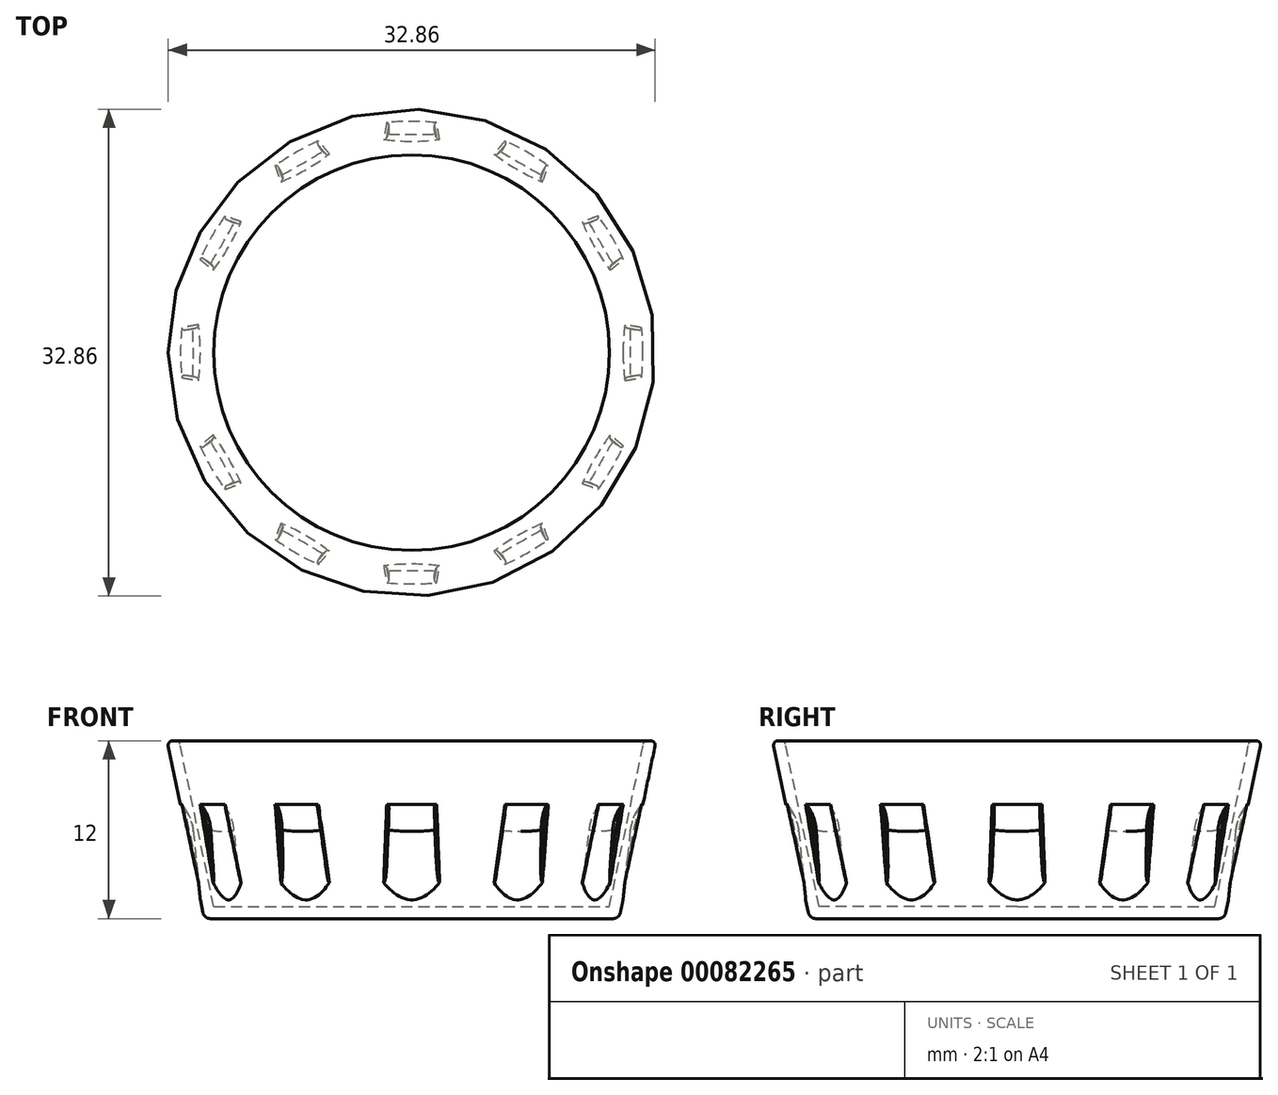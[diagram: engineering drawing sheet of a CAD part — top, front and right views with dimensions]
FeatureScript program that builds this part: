
annotation { "Feature Type Name" : "Feature", "Feature Type Description" : "" }
export const myFeature = defineFeature(function(context is Context, id is Id, definition is map)
    precondition{}
    {
        {
            var Q0;
            Q0=qCreatedBy(makeId("Front.planeOp"),FACE);
            var sketch = newSketch(context, id + "F0", { "sketchPlane" : qUnion([Q0])});
            skLineSegment(sketch, "E0", {"start": v(0, 0) * mm, "end": v(0, 12) * mm});
            skLineSegment(sketch, "E1.bottom", {"start": v(0, 12) * mm, "end": v(16.5, 12) * mm});
            skLineSegment(sketch, "E2", {"start": v(0, 0) * mm, "end": v(14, 0) * mm});
            skLineSegment(sketch, "E3", {"start": v(16.5, 12) * mm, "end": v(14, 0) * mm});
            skSolve(sketch);
        }
        {
            var Q0;
            Q0=qSketchRegion(id+"F0",true);
            var Q1;
            Q1=sQuery(id+"F0.wireOp",EDGE,"E0");
            revolve(context, id + "F1", {"entities" : qUnion([Q0]), "axis" : qUnion([Q1]), "revolveType" : RevolveType.FULL});
        }
        {
            var Q0;
            Q0=makeQuery(id+"F1.opRevolve","SWEPT_FACE",FACE,{"disambiguationData":[OSD([sQuery(id+"F0.wireOp",EDGE,"E1.bottom")])]});
            shell(context, id + "F2", {"entities" : qUnion([Q0]), "thickness" : 0.8 * mm});
        }
        {
            var Q0;
            Q0=makeQuery(id+"F2.opShell","OFFSET_EDGE",EDGE,{"disambiguationData":[OSD([sQuery(id+"F0.wireOp",EDGE,"E1.bottom"),sQuery(id+"F0.wireOp",EDGE,"E3")])]});
            var Q1;
            Q1=makeQuery(id+"F1.opRevolve","SWEPT_EDGE",EDGE,{"disambiguationData":[OSD([sQuery(id+"F0.wireOp",EDGE,"E1.bottom"),sQuery(id+"F0.wireOp",EDGE,"E3")])]});
            fillet(context, id + "F3", {"entities" : qUnion([Q0, Q1]), "radius" : .3 * mm, "tangentPropagation" : true, "allowEdgeOverflow" : false});
        }
        {
            var Q0;
            Q0=makeQuery(id+"F1.opRevolve","SWEPT_EDGE",EDGE,{"disambiguationData":[OSD([sQuery(id+"F0.wireOp",EDGE,"E2"),sQuery(id+"F0.wireOp",EDGE,"E3")])]});
            fillet(context, id + "F4", {"entities" : qUnion([Q0]), "radius" : .5 * mm, "tangentPropagation" : true, "allowEdgeOverflow" : false});
        }
        {
            var Q0;
            Q0=qCreatedBy(makeId("Front.planeOp"),FACE);
            var sketch = newSketch(context, id + "F5", { "sketchPlane" : qUnion([Q0])});
            skLineSegment(sketch, "E4", {"start": v(15.46, 12.9) * mm, "end": v(14.13, 0) * mm, "construction": true});
            skSolve(sketch);
        }
        {
            var Q0;
            Q0=sQuery(id+"F5.wireOp",EDGE,"E4");
            cPlane(context, id + "F6", {"entities" : qUnion([Q0]), "cplaneType" : CPlaneType.LINE_ANGLE, "offset" : 150 * mm, "angle" : 0 * degree, "width" : 150 * mm, "height" : 150 * mm});
        }
        {
            var Q0;
            Q0=qCreatedBy(id+"F6.planeOp",FACE);
            var sketch = newSketch(context, id + "F7", { "sketchPlane" : qUnion([Q0])});
            skPoint(sketch, "E5.middle", {"position": v(0, 9.22) * mm});
            skLineSegment(sketch, "E6.top", {"start": v(-1.5, 9.22) * mm, "end": v(1.5, 9.22) * mm});
            skLineSegment(sketch, "E7", {"start": v(1.5, 9.22) * mm, "end": v(1.8, 2.22) * mm});
            skLineSegment(sketch, "E8.MirrorCS", {"start": v(-1.5, 9.22) * mm, "end": v(-1.8, 2.22) * mm});
            skLineSegment(sketch, "E9", {"start": v(1.8, 2.22) * mm, "end": v(-1.8, 2.22) * mm});
            skSolve(sketch);
        }
        {
            var Q0;
            Q0=makeQuery(id+"F7.imprint","IMPRINT",FACE,{"disambiguationData":[TD([[makeQuery(id+"F7.imprint","IMPRINT",EDGE,{"derivedFrom":sQuery(id+"F7.wireOp",EDGE,"E6.top")}),-1.0]])]});
            extrude(context, id + "F8", {"entities" : qUnion([Q0]), "oppositeDirection" : true, "depth" : 1.04 * mm, "hasDraft" : true, "draftAngle" : 3 * degree});
        }
        {
            var Q0;
            Q0=makeQuery(id+"F8.opExtrude","SWEPT_BODY",BODY,{"disambiguationData":[OSD([sQuery(id+"F7.wireOp",EDGE,"E6.top"),sQuery(id+"F7.wireOp",EDGE,"E7"),sQuery(id+"F7.wireOp",EDGE,"E8.MirrorCS"),sQuery(id+"F7.wireOp",EDGE,"E9")])]});
            var Q1;
            {var subQ0=sQuery(id+"F0.wireOp",EDGE,"E3");Q1=makeQuery(id+"F4.opFillet","BLEND_EDGE",EDGE,{"blendedFrom":[makeQuery(id+"F1.opRevolve","SWEPT_EDGE",EDGE,{"disambiguationData":[OSD([sQuery(id+"F0.wireOp",EDGE,"E2"),subQ0])]}),makeQuery(id+"F1.opRevolve","SWEPT_FACE",FACE,{"disambiguationData":[OSD([subQ0])]})],"blendedInto":[makeQuery(id+"F1.opRevolve","SWEPT_FACE",FACE,{"disambiguationData":[OSD([subQ0])]})]});}
            circularPattern(context, id + "F9", {"entities" : qUnion([Q0]), "axis" : qUnion([Q1]), "angle" : 30 * degree, "instanceCount" : 12});
        }
        {
            var Q0;
            Q0=makeQuery(id+"F9.opPattern","COPY",BODY,{"derivedFrom":makeQuery(id+"F8.opExtrude","SWEPT_BODY",BODY,{"disambiguationData":[OSD([sQuery(id+"F7.wireOp",EDGE,"E6.top"),sQuery(id+"F7.wireOp",EDGE,"E7"),sQuery(id+"F7.wireOp",EDGE,"E8.MirrorCS"),sQuery(id+"F7.wireOp",EDGE,"E9")])]}),"instanceName":"17"});
            var Q1;
            Q1=makeQuery(id+"F9.opPattern","COPY",BODY,{"derivedFrom":makeQuery(id+"F8.opExtrude","SWEPT_BODY",BODY,{"disambiguationData":[OSD([sQuery(id+"F7.wireOp",EDGE,"E6.top"),sQuery(id+"F7.wireOp",EDGE,"E7"),sQuery(id+"F7.wireOp",EDGE,"E8.MirrorCS"),sQuery(id+"F7.wireOp",EDGE,"E9")])]}),"instanceName":"16"});
            var Q2;
            Q2=makeQuery(id+"F9.opPattern","COPY",BODY,{"derivedFrom":makeQuery(id+"F8.opExtrude","SWEPT_BODY",BODY,{"disambiguationData":[OSD([sQuery(id+"F7.wireOp",EDGE,"E6.top"),sQuery(id+"F7.wireOp",EDGE,"E7"),sQuery(id+"F7.wireOp",EDGE,"E8.MirrorCS"),sQuery(id+"F7.wireOp",EDGE,"E9")])]}),"instanceName":"15"});
            var Q3;
            Q3=makeQuery(id+"F9.opPattern","COPY",BODY,{"derivedFrom":makeQuery(id+"F8.opExtrude","SWEPT_BODY",BODY,{"disambiguationData":[OSD([sQuery(id+"F7.wireOp",EDGE,"E6.top"),sQuery(id+"F7.wireOp",EDGE,"E7"),sQuery(id+"F7.wireOp",EDGE,"E8.MirrorCS"),sQuery(id+"F7.wireOp",EDGE,"E9")])]}),"instanceName":"14"});
            var Q4;
            Q4=makeQuery(id+"F9.opPattern","COPY",BODY,{"derivedFrom":makeQuery(id+"F8.opExtrude","SWEPT_BODY",BODY,{"disambiguationData":[OSD([sQuery(id+"F7.wireOp",EDGE,"E6.top"),sQuery(id+"F7.wireOp",EDGE,"E7"),sQuery(id+"F7.wireOp",EDGE,"E8.MirrorCS"),sQuery(id+"F7.wireOp",EDGE,"E9")])]}),"instanceName":"13"});
            var Q5;
            Q5=makeQuery(id+"F9.opPattern","COPY",BODY,{"derivedFrom":makeQuery(id+"F8.opExtrude","SWEPT_BODY",BODY,{"disambiguationData":[OSD([sQuery(id+"F7.wireOp",EDGE,"E6.top"),sQuery(id+"F7.wireOp",EDGE,"E7"),sQuery(id+"F7.wireOp",EDGE,"E8.MirrorCS"),sQuery(id+"F7.wireOp",EDGE,"E9")])]}),"instanceName":"12"});
            var Q6;
            Q6=makeQuery(id+"F9.opPattern","COPY",BODY,{"derivedFrom":makeQuery(id+"F8.opExtrude","SWEPT_BODY",BODY,{"disambiguationData":[OSD([sQuery(id+"F7.wireOp",EDGE,"E6.top"),sQuery(id+"F7.wireOp",EDGE,"E7"),sQuery(id+"F7.wireOp",EDGE,"E8.MirrorCS"),sQuery(id+"F7.wireOp",EDGE,"E9")])]}),"instanceName":"11"});
            var Q7;
            Q7=makeQuery(id+"F9.opPattern","COPY",BODY,{"derivedFrom":makeQuery(id+"F8.opExtrude","SWEPT_BODY",BODY,{"disambiguationData":[OSD([sQuery(id+"F7.wireOp",EDGE,"E6.top"),sQuery(id+"F7.wireOp",EDGE,"E7"),sQuery(id+"F7.wireOp",EDGE,"E8.MirrorCS"),sQuery(id+"F7.wireOp",EDGE,"E9")])]}),"instanceName":"10"});
            var Q8;
            Q8=makeQuery(id+"F9.opPattern","COPY",BODY,{"derivedFrom":makeQuery(id+"F8.opExtrude","SWEPT_BODY",BODY,{"disambiguationData":[OSD([sQuery(id+"F7.wireOp",EDGE,"E6.top"),sQuery(id+"F7.wireOp",EDGE,"E7"),sQuery(id+"F7.wireOp",EDGE,"E8.MirrorCS"),sQuery(id+"F7.wireOp",EDGE,"E9")])]}),"instanceName":"9"});
            var Q9;
            Q9=makeQuery(id+"F9.opPattern","COPY",BODY,{"derivedFrom":makeQuery(id+"F8.opExtrude","SWEPT_BODY",BODY,{"disambiguationData":[OSD([sQuery(id+"F7.wireOp",EDGE,"E6.top"),sQuery(id+"F7.wireOp",EDGE,"E7"),sQuery(id+"F7.wireOp",EDGE,"E8.MirrorCS"),sQuery(id+"F7.wireOp",EDGE,"E9")])]}),"instanceName":"8"});
            var Q10;
            Q10=makeQuery(id+"F9.opPattern","COPY",BODY,{"derivedFrom":makeQuery(id+"F8.opExtrude","SWEPT_BODY",BODY,{"disambiguationData":[OSD([sQuery(id+"F7.wireOp",EDGE,"E6.top"),sQuery(id+"F7.wireOp",EDGE,"E7"),sQuery(id+"F7.wireOp",EDGE,"E8.MirrorCS"),sQuery(id+"F7.wireOp",EDGE,"E9")])]}),"instanceName":"7"});
            var Q11;
            Q11=makeQuery(id+"F9.opPattern","COPY",BODY,{"derivedFrom":makeQuery(id+"F8.opExtrude","SWEPT_BODY",BODY,{"disambiguationData":[OSD([sQuery(id+"F7.wireOp",EDGE,"E6.top"),sQuery(id+"F7.wireOp",EDGE,"E7"),sQuery(id+"F7.wireOp",EDGE,"E8.MirrorCS"),sQuery(id+"F7.wireOp",EDGE,"E9")])]}),"instanceName":"6"});
            var Q12;
            Q12=makeQuery(id+"F9.opPattern","COPY",BODY,{"derivedFrom":makeQuery(id+"F8.opExtrude","SWEPT_BODY",BODY,{"disambiguationData":[OSD([sQuery(id+"F7.wireOp",EDGE,"E6.top"),sQuery(id+"F7.wireOp",EDGE,"E7"),sQuery(id+"F7.wireOp",EDGE,"E8.MirrorCS"),sQuery(id+"F7.wireOp",EDGE,"E9")])]}),"instanceName":"5"});
            var Q13;
            Q13=makeQuery(id+"F9.opPattern","COPY",BODY,{"derivedFrom":makeQuery(id+"F8.opExtrude","SWEPT_BODY",BODY,{"disambiguationData":[OSD([sQuery(id+"F7.wireOp",EDGE,"E6.top"),sQuery(id+"F7.wireOp",EDGE,"E7"),sQuery(id+"F7.wireOp",EDGE,"E8.MirrorCS"),sQuery(id+"F7.wireOp",EDGE,"E9")])]}),"instanceName":"4"});
            var Q14;
            Q14=makeQuery(id+"F9.opPattern","COPY",BODY,{"derivedFrom":makeQuery(id+"F8.opExtrude","SWEPT_BODY",BODY,{"disambiguationData":[OSD([sQuery(id+"F7.wireOp",EDGE,"E6.top"),sQuery(id+"F7.wireOp",EDGE,"E7"),sQuery(id+"F7.wireOp",EDGE,"E8.MirrorCS"),sQuery(id+"F7.wireOp",EDGE,"E9")])]}),"instanceName":"3"});
            var Q15;
            Q15=makeQuery(id+"F9.opPattern","COPY",BODY,{"derivedFrom":makeQuery(id+"F8.opExtrude","SWEPT_BODY",BODY,{"disambiguationData":[OSD([sQuery(id+"F7.wireOp",EDGE,"E6.top"),sQuery(id+"F7.wireOp",EDGE,"E7"),sQuery(id+"F7.wireOp",EDGE,"E8.MirrorCS"),sQuery(id+"F7.wireOp",EDGE,"E9")])]}),"instanceName":"2"});
            var Q16;
            Q16=makeQuery(id+"F9.opPattern","COPY",BODY,{"derivedFrom":makeQuery(id+"F8.opExtrude","SWEPT_BODY",BODY,{"disambiguationData":[OSD([sQuery(id+"F7.wireOp",EDGE,"E6.top"),sQuery(id+"F7.wireOp",EDGE,"E7"),sQuery(id+"F7.wireOp",EDGE,"E8.MirrorCS"),sQuery(id+"F7.wireOp",EDGE,"E9")])]}),"instanceName":"1"});
            var Q17;
            Q17=makeQuery(id+"F8.opExtrude","SWEPT_BODY",BODY,{"disambiguationData":[OSD([sQuery(id+"F7.wireOp",EDGE,"E6.top"),sQuery(id+"F7.wireOp",EDGE,"E7"),sQuery(id+"F7.wireOp",EDGE,"E8.MirrorCS"),sQuery(id+"F7.wireOp",EDGE,"E9")])]});
            var Q18;
            Q18=makeQuery(id+"F1.opRevolve","SWEPT_BODY",BODY,{"disambiguationData":[OSD([sQuery(id+"F0.wireOp",EDGE,"E0"),sQuery(id+"F0.wireOp",EDGE,"E1.bottom"),sQuery(id+"F0.wireOp",EDGE,"E2"),sQuery(id+"F0.wireOp",EDGE,"E3")])]});
            booleanBodies(context, id + "F10", {"operationType" : BooleanOperationType.SUBTRACTION, "tools" : qUnion([Q0, Q1, Q2, Q3, Q4, Q5, Q6, Q7, Q8, Q9, Q10, Q11, Q12, Q13, Q14, Q15, Q16, Q17]), "targets" : qUnion([Q18])});
        }
        {
            var Q0;
            Q0=makeQuery(id+"F10.opBoolean","COPY",EDGE,{"derivedFrom":makeQuery(id+"F9.opPattern","COPY",EDGE,{"derivedFrom":makeQuery(id+"F8.opExtrude","CAP_EDGE",EDGE,{"disambiguationData":[OSD([sQuery(id+"F7.wireOp",EDGE,"E6.top")])],"isStart":true}),"instanceName":"6"})});
            var Q1;
            Q1=makeQuery(id+"F10.opBoolean","COPY",EDGE,{"derivedFrom":makeQuery(id+"F9.opPattern","COPY",EDGE,{"derivedFrom":makeQuery(id+"F8.opExtrude","CAP_EDGE",EDGE,{"disambiguationData":[OSD([sQuery(id+"F7.wireOp",EDGE,"E6.top")])],"isStart":true}),"instanceName":"7"})});
            var Q2;
            Q2=makeQuery(id+"F10.opBoolean","COPY",EDGE,{"derivedFrom":makeQuery(id+"F9.opPattern","COPY",EDGE,{"derivedFrom":makeQuery(id+"F8.opExtrude","CAP_EDGE",EDGE,{"disambiguationData":[OSD([sQuery(id+"F7.wireOp",EDGE,"E6.top")])],"isStart":true}),"instanceName":"5"})});
            var Q3;
            Q3=makeQuery(id+"F10.opBoolean","COPY",EDGE,{"derivedFrom":makeQuery(id+"F9.opPattern","COPY",EDGE,{"derivedFrom":makeQuery(id+"F8.opExtrude","CAP_EDGE",EDGE,{"disambiguationData":[OSD([sQuery(id+"F7.wireOp",EDGE,"E6.top")])],"isStart":true}),"instanceName":"4"})});
            var Q4;
            Q4=makeQuery(id+"F10.opBoolean","COPY",EDGE,{"derivedFrom":makeQuery(id+"F9.opPattern","COPY",EDGE,{"derivedFrom":makeQuery(id+"F8.opExtrude","CAP_EDGE",EDGE,{"disambiguationData":[OSD([sQuery(id+"F7.wireOp",EDGE,"E6.top")])],"isStart":true}),"instanceName":"8"})});
            var Q5;
            Q5=makeQuery(id+"F10.opBoolean","COPY",EDGE,{"derivedFrom":makeQuery(id+"F9.opPattern","COPY",EDGE,{"derivedFrom":makeQuery(id+"F8.opExtrude","CAP_EDGE",EDGE,{"disambiguationData":[OSD([sQuery(id+"F7.wireOp",EDGE,"E6.top")])],"isStart":true}),"instanceName":"9"})});
            var Q6;
            Q6=makeQuery(id+"F10.opBoolean","COPY",EDGE,{"derivedFrom":makeQuery(id+"F9.opPattern","COPY",EDGE,{"derivedFrom":makeQuery(id+"F8.opExtrude","CAP_EDGE",EDGE,{"disambiguationData":[OSD([sQuery(id+"F7.wireOp",EDGE,"E6.top")])],"isStart":true}),"instanceName":"10"})});
            var Q7;
            Q7=makeQuery(id+"F10.opBoolean","COPY",EDGE,{"derivedFrom":makeQuery(id+"F9.opPattern","COPY",EDGE,{"derivedFrom":makeQuery(id+"F8.opExtrude","CAP_EDGE",EDGE,{"disambiguationData":[OSD([sQuery(id+"F7.wireOp",EDGE,"E6.top")])],"isStart":true}),"instanceName":"11"})});
            var Q8;
            Q8=makeQuery(id+"F10.opBoolean","COPY",EDGE,{"derivedFrom":makeQuery(id+"F9.opPattern","COPY",EDGE,{"derivedFrom":makeQuery(id+"F8.opExtrude","CAP_EDGE",EDGE,{"disambiguationData":[OSD([sQuery(id+"F7.wireOp",EDGE,"E6.top")])],"isStart":true}),"instanceName":"12"})});
            var Q9;
            Q9=makeQuery(id+"F10.opBoolean","COPY",EDGE,{"derivedFrom":makeQuery(id+"F9.opPattern","COPY",EDGE,{"derivedFrom":makeQuery(id+"F8.opExtrude","CAP_EDGE",EDGE,{"disambiguationData":[OSD([sQuery(id+"F7.wireOp",EDGE,"E6.top")])],"isStart":true}),"instanceName":"13"})});
            var Q10;
            Q10=makeQuery(id+"F10.opBoolean","COPY",EDGE,{"derivedFrom":makeQuery(id+"F9.opPattern","COPY",EDGE,{"derivedFrom":makeQuery(id+"F8.opExtrude","CAP_EDGE",EDGE,{"disambiguationData":[OSD([sQuery(id+"F7.wireOp",EDGE,"E6.top")])],"isStart":true}),"instanceName":"3"})});
            var Q11;
            Q11=makeQuery(id+"F10.opBoolean","COPY",EDGE,{"derivedFrom":makeQuery(id+"F9.opPattern","COPY",EDGE,{"derivedFrom":makeQuery(id+"F8.opExtrude","CAP_EDGE",EDGE,{"disambiguationData":[OSD([sQuery(id+"F7.wireOp",EDGE,"E6.top")])],"isStart":true}),"instanceName":"2"})});
            var Q12;
            Q12=makeQuery(id+"F10.opBoolean","COPY",EDGE,{"derivedFrom":makeQuery(id+"F9.opPattern","COPY",EDGE,{"derivedFrom":makeQuery(id+"F8.opExtrude","CAP_EDGE",EDGE,{"disambiguationData":[OSD([sQuery(id+"F7.wireOp",EDGE,"E6.top")])],"isStart":true}),"instanceName":"1"})});
            var Q13;
            Q13=makeQuery(id+"F10.opBoolean","COPY",EDGE,{"derivedFrom":makeQuery(id+"F8.opExtrude","CAP_EDGE",EDGE,{"disambiguationData":[OSD([sQuery(id+"F7.wireOp",EDGE,"E6.top")])],"isStart":true})});
            var Q14;
            Q14=makeQuery(id+"F10.opBoolean","COPY",EDGE,{"derivedFrom":makeQuery(id+"F9.opPattern","COPY",EDGE,{"derivedFrom":makeQuery(id+"F8.opExtrude","CAP_EDGE",EDGE,{"disambiguationData":[OSD([sQuery(id+"F7.wireOp",EDGE,"E6.top")])],"isStart":true}),"instanceName":"17"})});
            var Q15;
            Q15=makeQuery(id+"F10.opBoolean","COPY",EDGE,{"derivedFrom":makeQuery(id+"F9.opPattern","COPY",EDGE,{"derivedFrom":makeQuery(id+"F8.opExtrude","CAP_EDGE",EDGE,{"disambiguationData":[OSD([sQuery(id+"F7.wireOp",EDGE,"E6.top")])],"isStart":true}),"instanceName":"16"})});
            var Q16;
            Q16=makeQuery(id+"F10.opBoolean","COPY",EDGE,{"derivedFrom":makeQuery(id+"F9.opPattern","COPY",EDGE,{"derivedFrom":makeQuery(id+"F8.opExtrude","CAP_EDGE",EDGE,{"disambiguationData":[OSD([sQuery(id+"F7.wireOp",EDGE,"E6.top")])],"isStart":true}),"instanceName":"15"})});
            var Q17;
            Q17=makeQuery(id+"F10.opBoolean","COPY",EDGE,{"derivedFrom":makeQuery(id+"F9.opPattern","COPY",EDGE,{"derivedFrom":makeQuery(id+"F8.opExtrude","CAP_EDGE",EDGE,{"disambiguationData":[OSD([sQuery(id+"F7.wireOp",EDGE,"E6.top")])],"isStart":true}),"instanceName":"14"})});
            fillet(context, id + "F11", {"entities" : qUnion([Q0, Q1, Q2, Q3, Q4, Q5, Q6, Q7, Q8, Q9, Q10, Q11, Q12, Q13, Q14, Q15, Q16, Q17]), "radius" : 3 * mm, "tangentPropagation" : true, "allowEdgeOverflow" : false});
        }
        {
            var Q0;
            Q0=makeQuery(id+"F10.opBoolean","INTERSECT",EDGE,{"derivedFrom":[makeQuery(id+"F1.opRevolve","SWEPT_FACE",FACE,{"disambiguationData":[OSD([sQuery(id+"F0.wireOp",EDGE,"E3")])]}),makeQuery(id+"F9.opPattern","COPY",FACE,{"derivedFrom":makeQuery(id+"F8.opExtrude","SWEPT_FACE",FACE,{"disambiguationData":[OSD([sQuery(id+"F7.wireOp",EDGE,"E8.MirrorCS")])]}),"instanceName":"2"})]});
            var Q1;
            Q1=makeQuery(id+"F10.opBoolean","INTERSECT",EDGE,{"derivedFrom":[makeQuery(id+"F1.opRevolve","SWEPT_FACE",FACE,{"disambiguationData":[OSD([sQuery(id+"F0.wireOp",EDGE,"E3")])]}),makeQuery(id+"F9.opPattern","COPY",FACE,{"derivedFrom":makeQuery(id+"F8.opExtrude","SWEPT_FACE",FACE,{"disambiguationData":[OSD([sQuery(id+"F7.wireOp",EDGE,"E7")])]}),"instanceName":"2"})]});
            var Q2;
            Q2=makeQuery(id+"F10.opBoolean","INTERSECT",EDGE,{"derivedFrom":[makeQuery(id+"F1.opRevolve","SWEPT_FACE",FACE,{"disambiguationData":[OSD([sQuery(id+"F0.wireOp",EDGE,"E3")])]}),makeQuery(id+"F9.opPattern","COPY",FACE,{"derivedFrom":makeQuery(id+"F8.opExtrude","SWEPT_FACE",FACE,{"disambiguationData":[OSD([sQuery(id+"F7.wireOp",EDGE,"E8.MirrorCS")])]}),"instanceName":"3"})]});
            var Q3;
            Q3=makeQuery(id+"F10.opBoolean","INTERSECT",EDGE,{"derivedFrom":[makeQuery(id+"F1.opRevolve","SWEPT_FACE",FACE,{"disambiguationData":[OSD([sQuery(id+"F0.wireOp",EDGE,"E3")])]}),makeQuery(id+"F9.opPattern","COPY",FACE,{"derivedFrom":makeQuery(id+"F8.opExtrude","SWEPT_FACE",FACE,{"disambiguationData":[OSD([sQuery(id+"F7.wireOp",EDGE,"E8.MirrorCS")])]}),"instanceName":"4"})]});
            var Q4;
            Q4=makeQuery(id+"F10.opBoolean","INTERSECT",EDGE,{"derivedFrom":[makeQuery(id+"F1.opRevolve","SWEPT_FACE",FACE,{"disambiguationData":[OSD([sQuery(id+"F0.wireOp",EDGE,"E3")])]}),makeQuery(id+"F9.opPattern","COPY",FACE,{"derivedFrom":makeQuery(id+"F8.opExtrude","SWEPT_FACE",FACE,{"disambiguationData":[OSD([sQuery(id+"F7.wireOp",EDGE,"E8.MirrorCS")])]}),"instanceName":"5"})]});
            var Q5;
            Q5=makeQuery(id+"F10.opBoolean","INTERSECT",EDGE,{"derivedFrom":[makeQuery(id+"F1.opRevolve","SWEPT_FACE",FACE,{"disambiguationData":[OSD([sQuery(id+"F0.wireOp",EDGE,"E3")])]}),makeQuery(id+"F9.opPattern","COPY",FACE,{"derivedFrom":makeQuery(id+"F8.opExtrude","SWEPT_FACE",FACE,{"disambiguationData":[OSD([sQuery(id+"F7.wireOp",EDGE,"E8.MirrorCS")])]}),"instanceName":"1"})]});
            var Q6;
            Q6=makeQuery(id+"F10.opBoolean","INTERSECT",EDGE,{"derivedFrom":[makeQuery(id+"F1.opRevolve","SWEPT_FACE",FACE,{"disambiguationData":[OSD([sQuery(id+"F0.wireOp",EDGE,"E3")])]}),makeQuery(id+"F9.opPattern","COPY",FACE,{"derivedFrom":makeQuery(id+"F8.opExtrude","SWEPT_FACE",FACE,{"disambiguationData":[OSD([sQuery(id+"F7.wireOp",EDGE,"E7")])]}),"instanceName":"1"})]});
            var Q7;
            Q7=makeQuery(id+"F10.opBoolean","INTERSECT",EDGE,{"derivedFrom":[makeQuery(id+"F1.opRevolve","SWEPT_FACE",FACE,{"disambiguationData":[OSD([sQuery(id+"F0.wireOp",EDGE,"E3")])]}),makeQuery(id+"F8.opExtrude","SWEPT_FACE",FACE,{"disambiguationData":[OSD([sQuery(id+"F7.wireOp",EDGE,"E7")])]})]});
            var Q8;
            Q8=makeQuery(id+"F10.opBoolean","INTERSECT",EDGE,{"derivedFrom":[makeQuery(id+"F1.opRevolve","SWEPT_FACE",FACE,{"disambiguationData":[OSD([sQuery(id+"F0.wireOp",EDGE,"E3")])]}),makeQuery(id+"F8.opExtrude","SWEPT_FACE",FACE,{"disambiguationData":[OSD([sQuery(id+"F7.wireOp",EDGE,"E8.MirrorCS")])]})]});
            var Q9;
            Q9=makeQuery(id+"F10.opBoolean","INTERSECT",EDGE,{"derivedFrom":[makeQuery(id+"F1.opRevolve","SWEPT_FACE",FACE,{"disambiguationData":[OSD([sQuery(id+"F0.wireOp",EDGE,"E3")])]}),makeQuery(id+"F9.opPattern","COPY",FACE,{"derivedFrom":makeQuery(id+"F8.opExtrude","SWEPT_FACE",FACE,{"disambiguationData":[OSD([sQuery(id+"F7.wireOp",EDGE,"E8.MirrorCS")])]}),"instanceName":"17"})]});
            var Q10;
            Q10=makeQuery(id+"F10.opBoolean","INTERSECT",EDGE,{"derivedFrom":[makeQuery(id+"F1.opRevolve","SWEPT_FACE",FACE,{"disambiguationData":[OSD([sQuery(id+"F0.wireOp",EDGE,"E3")])]}),makeQuery(id+"F9.opPattern","COPY",FACE,{"derivedFrom":makeQuery(id+"F8.opExtrude","SWEPT_FACE",FACE,{"disambiguationData":[OSD([sQuery(id+"F7.wireOp",EDGE,"E7")])]}),"instanceName":"17"})]});
            var Q11;
            Q11=makeQuery(id+"F10.opBoolean","INTERSECT",EDGE,{"derivedFrom":[makeQuery(id+"F1.opRevolve","SWEPT_FACE",FACE,{"disambiguationData":[OSD([sQuery(id+"F0.wireOp",EDGE,"E3")])]}),makeQuery(id+"F9.opPattern","COPY",FACE,{"derivedFrom":makeQuery(id+"F8.opExtrude","SWEPT_FACE",FACE,{"disambiguationData":[OSD([sQuery(id+"F7.wireOp",EDGE,"E7")])]}),"instanceName":"3"})]});
            var Q12;
            Q12=makeQuery(id+"F10.opBoolean","INTERSECT",EDGE,{"derivedFrom":[makeQuery(id+"F1.opRevolve","SWEPT_FACE",FACE,{"disambiguationData":[OSD([sQuery(id+"F0.wireOp",EDGE,"E3")])]}),makeQuery(id+"F9.opPattern","COPY",FACE,{"derivedFrom":makeQuery(id+"F8.opExtrude","SWEPT_FACE",FACE,{"disambiguationData":[OSD([sQuery(id+"F7.wireOp",EDGE,"E7")])]}),"instanceName":"4"})]});
            var Q13;
            Q13=makeQuery(id+"F10.opBoolean","INTERSECT",EDGE,{"derivedFrom":[makeQuery(id+"F1.opRevolve","SWEPT_FACE",FACE,{"disambiguationData":[OSD([sQuery(id+"F0.wireOp",EDGE,"E3")])]}),makeQuery(id+"F9.opPattern","COPY",FACE,{"derivedFrom":makeQuery(id+"F8.opExtrude","SWEPT_FACE",FACE,{"disambiguationData":[OSD([sQuery(id+"F7.wireOp",EDGE,"E7")])]}),"instanceName":"5"})]});
            var Q14;
            Q14=makeQuery(id+"F10.opBoolean","INTERSECT",EDGE,{"derivedFrom":[makeQuery(id+"F1.opRevolve","SWEPT_FACE",FACE,{"disambiguationData":[OSD([sQuery(id+"F0.wireOp",EDGE,"E3")])]}),makeQuery(id+"F9.opPattern","COPY",FACE,{"derivedFrom":makeQuery(id+"F8.opExtrude","SWEPT_FACE",FACE,{"disambiguationData":[OSD([sQuery(id+"F7.wireOp",EDGE,"E7")])]}),"instanceName":"6"})]});
            var Q15;
            Q15=makeQuery(id+"F10.opBoolean","INTERSECT",EDGE,{"derivedFrom":[makeQuery(id+"F1.opRevolve","SWEPT_FACE",FACE,{"disambiguationData":[OSD([sQuery(id+"F0.wireOp",EDGE,"E3")])]}),makeQuery(id+"F9.opPattern","COPY",FACE,{"derivedFrom":makeQuery(id+"F8.opExtrude","SWEPT_FACE",FACE,{"disambiguationData":[OSD([sQuery(id+"F7.wireOp",EDGE,"E8.MirrorCS")])]}),"instanceName":"6"})]});
            var Q16;
            Q16=makeQuery(id+"F10.opBoolean","INTERSECT",EDGE,{"derivedFrom":[makeQuery(id+"F1.opRevolve","SWEPT_FACE",FACE,{"disambiguationData":[OSD([sQuery(id+"F0.wireOp",EDGE,"E3")])]}),makeQuery(id+"F9.opPattern","COPY",FACE,{"derivedFrom":makeQuery(id+"F8.opExtrude","SWEPT_FACE",FACE,{"disambiguationData":[OSD([sQuery(id+"F7.wireOp",EDGE,"E7")])]}),"instanceName":"7"})]});
            var Q17;
            Q17=makeQuery(id+"F10.opBoolean","INTERSECT",EDGE,{"derivedFrom":[makeQuery(id+"F1.opRevolve","SWEPT_FACE",FACE,{"disambiguationData":[OSD([sQuery(id+"F0.wireOp",EDGE,"E3")])]}),makeQuery(id+"F9.opPattern","COPY",FACE,{"derivedFrom":makeQuery(id+"F8.opExtrude","SWEPT_FACE",FACE,{"disambiguationData":[OSD([sQuery(id+"F7.wireOp",EDGE,"E8.MirrorCS")])]}),"instanceName":"7"})]});
            var Q18;
            Q18=makeQuery(id+"F10.opBoolean","INTERSECT",EDGE,{"derivedFrom":[makeQuery(id+"F1.opRevolve","SWEPT_FACE",FACE,{"disambiguationData":[OSD([sQuery(id+"F0.wireOp",EDGE,"E3")])]}),makeQuery(id+"F9.opPattern","COPY",FACE,{"derivedFrom":makeQuery(id+"F8.opExtrude","SWEPT_FACE",FACE,{"disambiguationData":[OSD([sQuery(id+"F7.wireOp",EDGE,"E7")])]}),"instanceName":"8"})]});
            var Q19;
            Q19=makeQuery(id+"F10.opBoolean","INTERSECT",EDGE,{"derivedFrom":[makeQuery(id+"F1.opRevolve","SWEPT_FACE",FACE,{"disambiguationData":[OSD([sQuery(id+"F0.wireOp",EDGE,"E3")])]}),makeQuery(id+"F9.opPattern","COPY",FACE,{"derivedFrom":makeQuery(id+"F8.opExtrude","SWEPT_FACE",FACE,{"disambiguationData":[OSD([sQuery(id+"F7.wireOp",EDGE,"E8.MirrorCS")])]}),"instanceName":"8"})]});
            var Q20;
            Q20=makeQuery(id+"F10.opBoolean","INTERSECT",EDGE,{"derivedFrom":[makeQuery(id+"F1.opRevolve","SWEPT_FACE",FACE,{"disambiguationData":[OSD([sQuery(id+"F0.wireOp",EDGE,"E3")])]}),makeQuery(id+"F9.opPattern","COPY",FACE,{"derivedFrom":makeQuery(id+"F8.opExtrude","SWEPT_FACE",FACE,{"disambiguationData":[OSD([sQuery(id+"F7.wireOp",EDGE,"E7")])]}),"instanceName":"9"})]});
            var Q21;
            Q21=makeQuery(id+"F10.opBoolean","INTERSECT",EDGE,{"derivedFrom":[makeQuery(id+"F1.opRevolve","SWEPT_FACE",FACE,{"disambiguationData":[OSD([sQuery(id+"F0.wireOp",EDGE,"E3")])]}),makeQuery(id+"F9.opPattern","COPY",FACE,{"derivedFrom":makeQuery(id+"F8.opExtrude","SWEPT_FACE",FACE,{"disambiguationData":[OSD([sQuery(id+"F7.wireOp",EDGE,"E8.MirrorCS")])]}),"instanceName":"9"})]});
            var Q22;
            Q22=makeQuery(id+"F10.opBoolean","INTERSECT",EDGE,{"derivedFrom":[makeQuery(id+"F1.opRevolve","SWEPT_FACE",FACE,{"disambiguationData":[OSD([sQuery(id+"F0.wireOp",EDGE,"E3")])]}),makeQuery(id+"F9.opPattern","COPY",FACE,{"derivedFrom":makeQuery(id+"F8.opExtrude","SWEPT_FACE",FACE,{"disambiguationData":[OSD([sQuery(id+"F7.wireOp",EDGE,"E7")])]}),"instanceName":"10"})]});
            var Q23;
            Q23=makeQuery(id+"F10.opBoolean","INTERSECT",EDGE,{"derivedFrom":[makeQuery(id+"F1.opRevolve","SWEPT_FACE",FACE,{"disambiguationData":[OSD([sQuery(id+"F0.wireOp",EDGE,"E3")])]}),makeQuery(id+"F9.opPattern","COPY",FACE,{"derivedFrom":makeQuery(id+"F8.opExtrude","SWEPT_FACE",FACE,{"disambiguationData":[OSD([sQuery(id+"F7.wireOp",EDGE,"E8.MirrorCS")])]}),"instanceName":"10"})]});
            var Q24;
            Q24=makeQuery(id+"F10.opBoolean","INTERSECT",EDGE,{"derivedFrom":[makeQuery(id+"F1.opRevolve","SWEPT_FACE",FACE,{"disambiguationData":[OSD([sQuery(id+"F0.wireOp",EDGE,"E3")])]}),makeQuery(id+"F9.opPattern","COPY",FACE,{"derivedFrom":makeQuery(id+"F8.opExtrude","SWEPT_FACE",FACE,{"disambiguationData":[OSD([sQuery(id+"F7.wireOp",EDGE,"E7")])]}),"instanceName":"11"})]});
            var Q25;
            Q25=makeQuery(id+"F10.opBoolean","INTERSECT",EDGE,{"derivedFrom":[makeQuery(id+"F1.opRevolve","SWEPT_FACE",FACE,{"disambiguationData":[OSD([sQuery(id+"F0.wireOp",EDGE,"E3")])]}),makeQuery(id+"F9.opPattern","COPY",FACE,{"derivedFrom":makeQuery(id+"F8.opExtrude","SWEPT_FACE",FACE,{"disambiguationData":[OSD([sQuery(id+"F7.wireOp",EDGE,"E8.MirrorCS")])]}),"instanceName":"11"})]});
            var Q26;
            Q26=makeQuery(id+"F10.opBoolean","INTERSECT",EDGE,{"derivedFrom":[makeQuery(id+"F1.opRevolve","SWEPT_FACE",FACE,{"disambiguationData":[OSD([sQuery(id+"F0.wireOp",EDGE,"E3")])]}),makeQuery(id+"F9.opPattern","COPY",FACE,{"derivedFrom":makeQuery(id+"F8.opExtrude","SWEPT_FACE",FACE,{"disambiguationData":[OSD([sQuery(id+"F7.wireOp",EDGE,"E7")])]}),"instanceName":"12"})]});
            var Q27;
            Q27=makeQuery(id+"F10.opBoolean","INTERSECT",EDGE,{"derivedFrom":[makeQuery(id+"F1.opRevolve","SWEPT_FACE",FACE,{"disambiguationData":[OSD([sQuery(id+"F0.wireOp",EDGE,"E3")])]}),makeQuery(id+"F9.opPattern","COPY",FACE,{"derivedFrom":makeQuery(id+"F8.opExtrude","SWEPT_FACE",FACE,{"disambiguationData":[OSD([sQuery(id+"F7.wireOp",EDGE,"E8.MirrorCS")])]}),"instanceName":"12"})]});
            var Q28;
            Q28=makeQuery(id+"F10.opBoolean","INTERSECT",EDGE,{"derivedFrom":[makeQuery(id+"F1.opRevolve","SWEPT_FACE",FACE,{"disambiguationData":[OSD([sQuery(id+"F0.wireOp",EDGE,"E3")])]}),makeQuery(id+"F9.opPattern","COPY",FACE,{"derivedFrom":makeQuery(id+"F8.opExtrude","SWEPT_FACE",FACE,{"disambiguationData":[OSD([sQuery(id+"F7.wireOp",EDGE,"E7")])]}),"instanceName":"13"})]});
            var Q29;
            Q29=makeQuery(id+"F10.opBoolean","INTERSECT",EDGE,{"derivedFrom":[makeQuery(id+"F1.opRevolve","SWEPT_FACE",FACE,{"disambiguationData":[OSD([sQuery(id+"F0.wireOp",EDGE,"E3")])]}),makeQuery(id+"F9.opPattern","COPY",FACE,{"derivedFrom":makeQuery(id+"F8.opExtrude","SWEPT_FACE",FACE,{"disambiguationData":[OSD([sQuery(id+"F7.wireOp",EDGE,"E8.MirrorCS")])]}),"instanceName":"13"})]});
            var Q30;
            Q30=makeQuery(id+"F10.opBoolean","INTERSECT",EDGE,{"derivedFrom":[makeQuery(id+"F1.opRevolve","SWEPT_FACE",FACE,{"disambiguationData":[OSD([sQuery(id+"F0.wireOp",EDGE,"E3")])]}),makeQuery(id+"F9.opPattern","COPY",FACE,{"derivedFrom":makeQuery(id+"F8.opExtrude","SWEPT_FACE",FACE,{"disambiguationData":[OSD([sQuery(id+"F7.wireOp",EDGE,"E7")])]}),"instanceName":"14"})]});
            var Q31;
            Q31=makeQuery(id+"F10.opBoolean","INTERSECT",EDGE,{"derivedFrom":[makeQuery(id+"F1.opRevolve","SWEPT_FACE",FACE,{"disambiguationData":[OSD([sQuery(id+"F0.wireOp",EDGE,"E3")])]}),makeQuery(id+"F9.opPattern","COPY",FACE,{"derivedFrom":makeQuery(id+"F8.opExtrude","SWEPT_FACE",FACE,{"disambiguationData":[OSD([sQuery(id+"F7.wireOp",EDGE,"E8.MirrorCS")])]}),"instanceName":"14"})]});
            var Q32;
            Q32=makeQuery(id+"F10.opBoolean","INTERSECT",EDGE,{"derivedFrom":[makeQuery(id+"F1.opRevolve","SWEPT_FACE",FACE,{"disambiguationData":[OSD([sQuery(id+"F0.wireOp",EDGE,"E3")])]}),makeQuery(id+"F9.opPattern","COPY",FACE,{"derivedFrom":makeQuery(id+"F8.opExtrude","SWEPT_FACE",FACE,{"disambiguationData":[OSD([sQuery(id+"F7.wireOp",EDGE,"E7")])]}),"instanceName":"15"})]});
            var Q33;
            Q33=makeQuery(id+"F10.opBoolean","INTERSECT",EDGE,{"derivedFrom":[makeQuery(id+"F1.opRevolve","SWEPT_FACE",FACE,{"disambiguationData":[OSD([sQuery(id+"F0.wireOp",EDGE,"E3")])]}),makeQuery(id+"F9.opPattern","COPY",FACE,{"derivedFrom":makeQuery(id+"F8.opExtrude","SWEPT_FACE",FACE,{"disambiguationData":[OSD([sQuery(id+"F7.wireOp",EDGE,"E8.MirrorCS")])]}),"instanceName":"15"})]});
            var Q34;
            Q34=makeQuery(id+"F10.opBoolean","INTERSECT",EDGE,{"derivedFrom":[makeQuery(id+"F1.opRevolve","SWEPT_FACE",FACE,{"disambiguationData":[OSD([sQuery(id+"F0.wireOp",EDGE,"E3")])]}),makeQuery(id+"F9.opPattern","COPY",FACE,{"derivedFrom":makeQuery(id+"F8.opExtrude","SWEPT_FACE",FACE,{"disambiguationData":[OSD([sQuery(id+"F7.wireOp",EDGE,"E7")])]}),"instanceName":"16"})]});
            var Q35;
            Q35=makeQuery(id+"F10.opBoolean","INTERSECT",EDGE,{"derivedFrom":[makeQuery(id+"F1.opRevolve","SWEPT_FACE",FACE,{"disambiguationData":[OSD([sQuery(id+"F0.wireOp",EDGE,"E3")])]}),makeQuery(id+"F9.opPattern","COPY",FACE,{"derivedFrom":makeQuery(id+"F8.opExtrude","SWEPT_FACE",FACE,{"disambiguationData":[OSD([sQuery(id+"F7.wireOp",EDGE,"E8.MirrorCS")])]}),"instanceName":"16"})]});
            fillet(context, id + "F12", {"entities" : qUnion([Q0, Q1, Q2, Q3, Q4, Q5, Q6, Q7, Q8, Q9, Q10, Q11, Q12, Q13, Q14, Q15, Q16, Q17, Q18, Q19, Q20, Q21, Q22, Q23, Q24, Q25, Q26, Q27, Q28, Q29, Q30, Q31, Q32, Q33, Q34, Q35]), "radius" : .15 * mm, "tangentPropagation" : true, "allowEdgeOverflow" : false});
        }
    });
